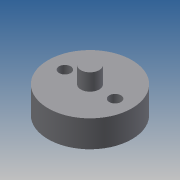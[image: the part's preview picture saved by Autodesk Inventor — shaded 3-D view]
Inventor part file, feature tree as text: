
AUTODESK INVENTOR PART (.ipt)
format: ipt  version: 2013 (Build 170138000, 138)  size: 113,664 bytes
history: native  units: mm
features: extrude x4, sketch x4, chamfer x1
ambient origin geometry x8: Origin, YZ Plane, XZ Plane, XY Plane, X Axis, Y Axis, Z Axis, Center Point
bodies: Solid1 (feature_tree)
feature tree (9):
  extrude  "Extrusion1"  Depth=8.0mm TaperAngle=0.0deg
  extrude  "Extrusion2"  Depth=5.0mm TaperAngle=0.0deg
  extrude  "Extrusion3"  Depth=7.5mm
  extrude  "Extrusion4"  Depth=5.0mm TaperAngle=0.0deg
  chamfer  "Chamfer1"  Distance=5.5mm
  sketch  "Sketch1"  dims[d0=25.0mm d2=8.0mm d3=0.0mm]
  sketch  "Sketch2"  dims[d4=5.5mm d6=5.0mm d7=0.0mm]
  sketch  "Sketch3"  dims[d8=7.5mm d9=7.5mm]
  sketch  "Sketch4"  dims[d10=3.5mm d11=5.0mm d12=0.0mm d13=5.5mm d14=4.0mm d15=0.0mm d16=2.0mm d17=2.0mm d18=45.0deg]
